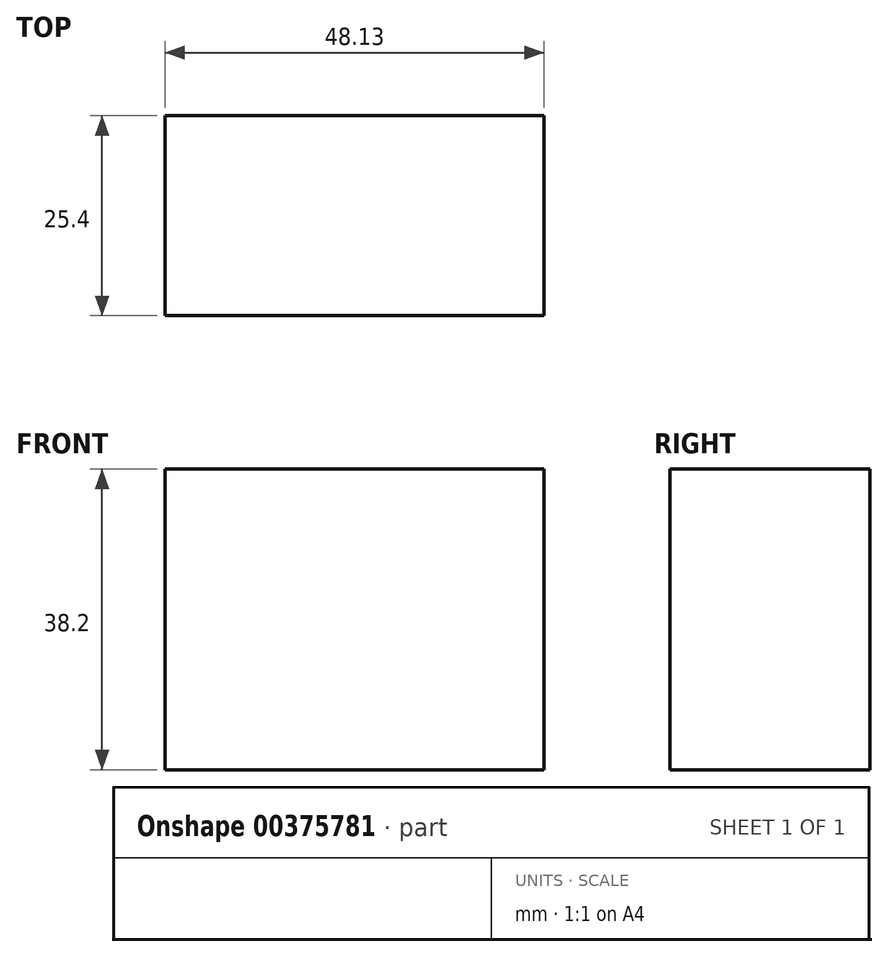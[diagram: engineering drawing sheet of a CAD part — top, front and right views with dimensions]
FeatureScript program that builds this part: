
annotation { "Feature Type Name" : "Feature", "Feature Type Description" : "" }
export const myFeature = defineFeature(function(context is Context, id is Id, definition is map)
    precondition{}
    {
        {
            var Q0;
            Q0=qCreatedBy(makeId("Front.planeOp"),FACE);
            var sketch = newSketch(context, id + "F0", { "sketchPlane" : qUnion([Q0])});
            skLineSegment(sketch, "E0.bottom", {"start": v(0, 0) * mm, "end": v(48.13, 0) * mm});
            skLineSegment(sketch, "E0.top", {"start": v(0, 38.2) * mm, "end": v(48.13, 38.2) * mm});
            skLineSegment(sketch, "E0.left", {"start": v(0, 0) * mm, "end": v(0, 38.2) * mm});
            skLineSegment(sketch, "E0.right", {"start": v(48.13, 0) * mm, "end": v(48.13, 38.2) * mm});
            skSolve(sketch);
        }
        {
            var Q0;
            Q0=makeQuery(id+"F0.imprint","IMPRINT",FACE,{"disambiguationData":[TD([[makeQuery(id+"F0.imprint","IMPRINT",EDGE,{"derivedFrom":sQuery(id+"F0.wireOp",EDGE,"E0.bottom")}),1.0]])]});
            extrude(context, id + "F1", {"entities" : qUnion([Q0]), "oppositeDirection" : true, "depth" : 25.4 * mm});
        }
    });
